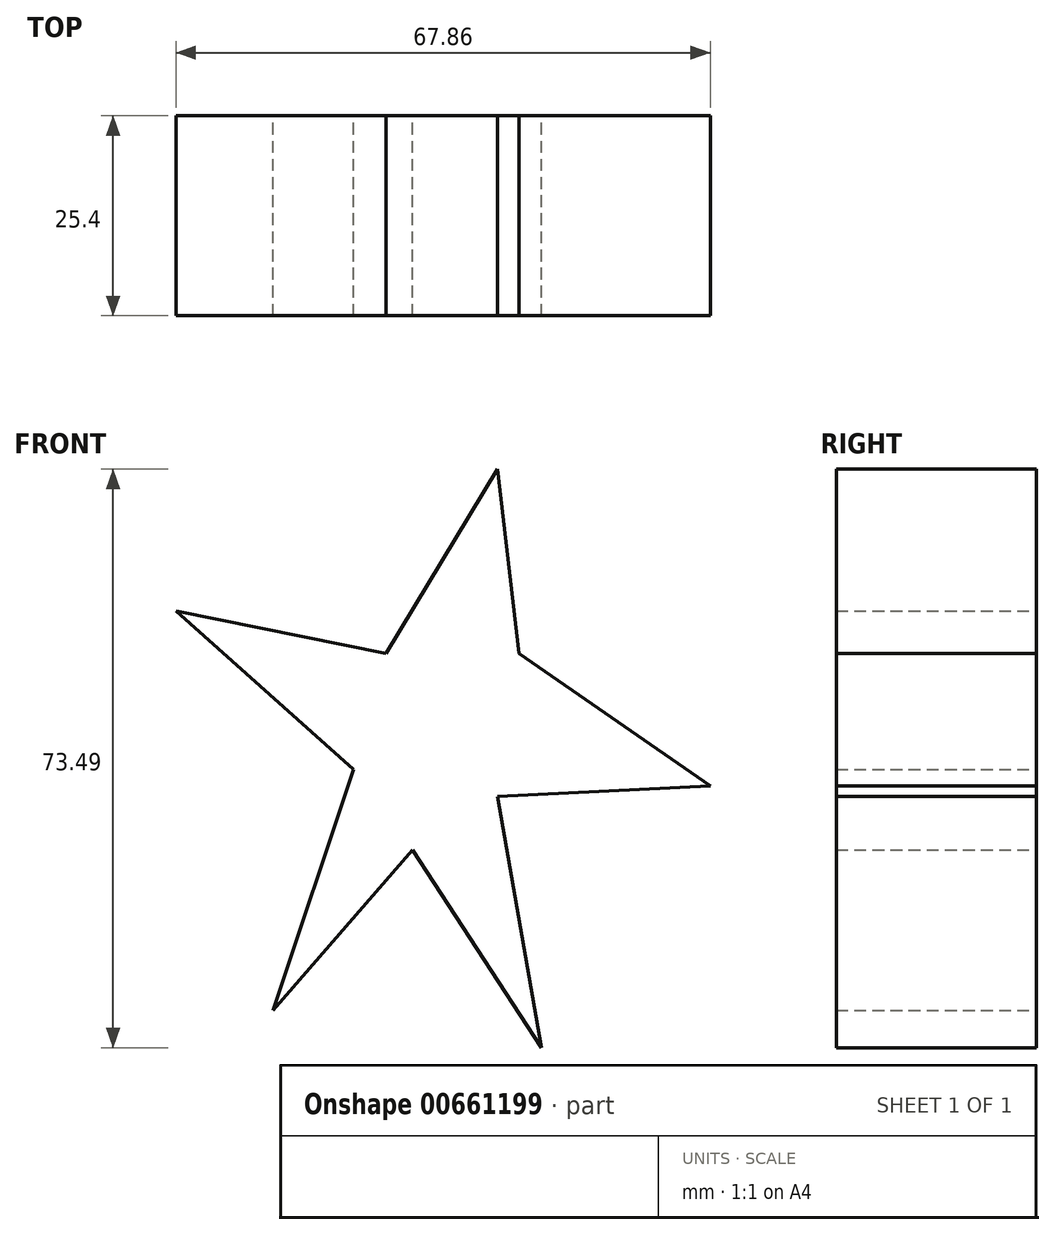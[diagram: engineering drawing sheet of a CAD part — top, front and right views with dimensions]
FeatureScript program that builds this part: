
annotation { "Feature Type Name" : "Feature", "Feature Type Description" : "" }
export const myFeature = defineFeature(function(context is Context, id is Id, definition is map)
    precondition{}
    {
        {
            var Q0;
            Q0=qCreatedBy(makeId("Front.planeOp"),FACE);
            var sketch = newSketch(context, id + "F0", { "sketchPlane" : qUnion([Q0])});
            skLineSegment(sketch, "E0", {"start": v(0, 0) * mm, "end": v(-17.41, 26.72) * mm});
            skLineSegment(sketch, "E1", {"start": v(-17.41, 26.72) * mm, "end": v(-35.13, 6.3) * mm});
            skLineSegment(sketch, "E2", {"start": v(-35.13, 6.3) * mm, "end": v(-24.92, 36.93) * mm});
            skLineSegment(sketch, "E3", {"start": v(-24.92, 36.93) * mm, "end": v(-47.44, 57.04) * mm});
            skLineSegment(sketch, "E4", {"start": v(-47.44, 57.04) * mm, "end": v(-20.78, 51.64) * mm});
            skLineSegment(sketch, "E5", {"start": v(-20.78, 51.64) * mm, "end": v(-6.6, 75.06) * mm});
            skLineSegment(sketch, "E6", {"start": v(-6.6, 75.06) * mm, "end": v(-3.9, 51.64) * mm});
            skLineSegment(sketch, "E7", {"start": v(-3.9, 51.64) * mm, "end": v(20.42, 34.83) * mm});
            skLineSegment(sketch, "E8", {"start": v(20.42, 34.83) * mm, "end": v(-6.6, 33.5) * mm});
            skLineSegment(sketch, "E9", {"start": v(-6.6, 33.5) * mm, "end": v(-1.02, 1.57) * mm});
            skSolve(sketch);
        }
        {
            var Q0;
            {var subQ0=sQuery(id+"F0.wireOp",EDGE,"E1");Q0=makeQuery(id+"F0.imprint","IMPRINT",FACE,{"disambiguationData":[TD([[makeQuery(id+"F0.imprint","IMPRINT",EDGE,{"derivedFrom":subQ0}),-1.0]])]});}
            extrude(context, id + "F1", {"entities" : qUnion([Q0]), "depth" : 25.4 * mm, "offsetDistance" : 25.4 * mm});
        }
    });
